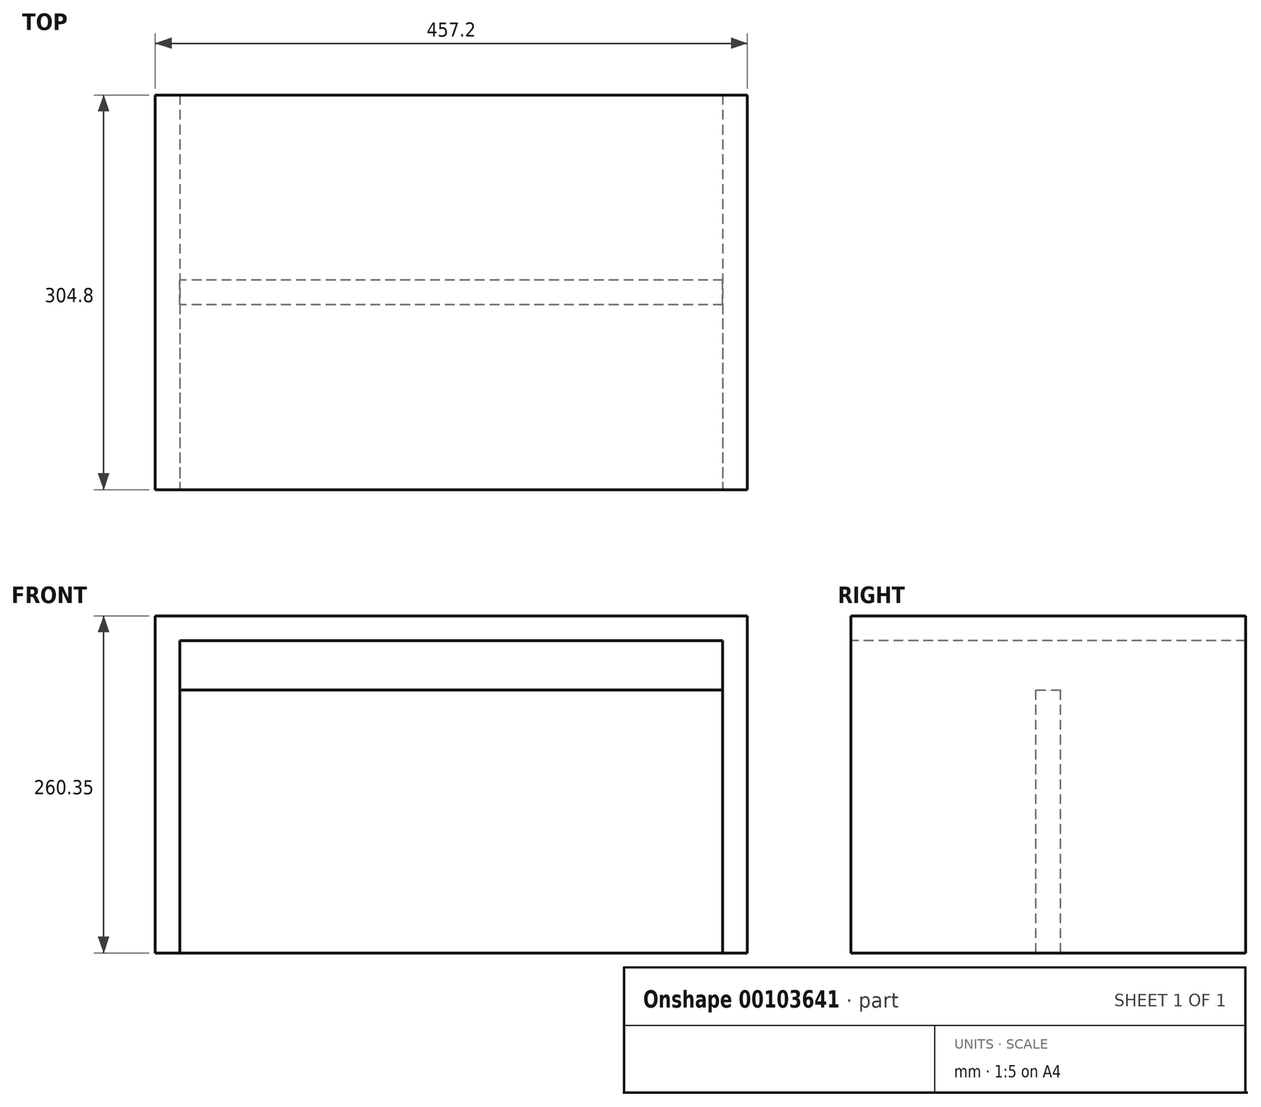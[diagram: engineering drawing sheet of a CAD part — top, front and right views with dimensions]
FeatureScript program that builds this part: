
annotation { "Feature Type Name" : "Feature", "Feature Type Description" : "" }
export const myFeature = defineFeature(function(context is Context, id is Id, definition is map)
    precondition{}
    {
        {
            var Q0;
            Q0=qCreatedBy(makeId("Top.planeOp"),FACE);
            var sketch = newSketch(context, id + "F0", { "sketchPlane" : qUnion([Q0])});
            skLineSegment(sketch, "E0.bottom", {"start": v(-228.6, 152.4) * mm, "end": v(228.6, 152.4) * mm});
            skLineSegment(sketch, "E0.top", {"start": v(-228.6, -152.4) * mm, "end": v(228.6, -152.4) * mm});
            skLineSegment(sketch, "E0.left", {"start": v(-228.6, 152.4) * mm, "end": v(-228.6, -152.4) * mm});
            skLineSegment(sketch, "E0.right", {"start": v(228.6, 152.4) * mm, "end": v(228.6, -152.4) * mm});
            skSolve(sketch);
        }
        {
            var Q0;
            Q0=makeQuery(id+"F0.imprint","IMPRINT",FACE,{"disambiguationData":[TD([[makeQuery(id+"F0.imprint","IMPRINT",EDGE,{"derivedFrom":sQuery(id+"F0.wireOp",EDGE,"E0.bottom")}),-1.0]])]});
            extrude(context, id + "F1", {"entities" : qUnion([Q0]), "depth" : 260.35 * mm});
        }
        {
            var Q0;
            Q0=makeQuery(id+"F1.opExtrude","SWEPT_FACE",FACE,{"disambiguationData":[OSD([sQuery(id+"F0.wireOp",EDGE,"E0.bottom")])]});
            var Q1;
            Q1=makeQuery(id+"F1.opExtrude","SWEPT_FACE",FACE,{"disambiguationData":[OSD([sQuery(id+"F0.wireOp",EDGE,"E0.top")])]});
            var Q2;
            Q2=makeQuery(id+"F1.opExtrude","CAP_FACE",FACE,{"disambiguationData":[OSD([sQuery(id+"F0.wireOp",EDGE,"E0.bottom"),sQuery(id+"F0.wireOp",EDGE,"E0.top"),sQuery(id+"F0.wireOp",EDGE,"E0.left"),sQuery(id+"F0.wireOp",EDGE,"E0.right")])],"isStart":true});
            shell(context, id + "F2", {"entities" : qUnion([Q0, Q1, Q2]), "thickness" : 19.05 * mm});
        }
        {
            var Q0;
            Q0=qCreatedBy(makeId("Front.planeOp"),FACE);
            var sketch = newSketch(context, id + "F3", { "sketchPlane" : qUnion([Q0])});
            skLineSegment(sketch, "E1.left", {"start": v(209.55, 0) * mm, "end": v(209.55, 0) * mm});
            skLineSegment(sketch, "E1.right", {"start": v(-208.76, 0) * mm, "end": v(-208.76, 0) * mm});
            skLineSegment(sketch, "E2.bottom", {"start": v(209.55, 0) * mm, "end": v(-209.55, 0) * mm});
            skLineSegment(sketch, "E2.top", {"start": v(209.55, 203.2) * mm, "end": v(-209.55, 203.2) * mm});
            skLineSegment(sketch, "E2.left", {"start": v(209.55, 0) * mm, "end": v(209.55, 203.2) * mm});
            skLineSegment(sketch, "E2.right", {"start": v(-209.55, 0) * mm, "end": v(-209.55, 203.2) * mm});
            skLineSegment(sketch, "E3.0", {"start": v(209.55, 241.3) * mm, "end": v(209.55, 0) * mm, "construction": true});
            skSolve(sketch);
        }
        {
            var Q0;
            Q0=qSketchRegion(id+"F3",true);
            extrude(context, id + "F4", {"entities" : qUnion([Q0]), "operationType" : NewBodyOperationType.ADD, "endBound" : BoundingType.SYMMETRIC, "depth" : 19.05 * mm});
        }
    });
